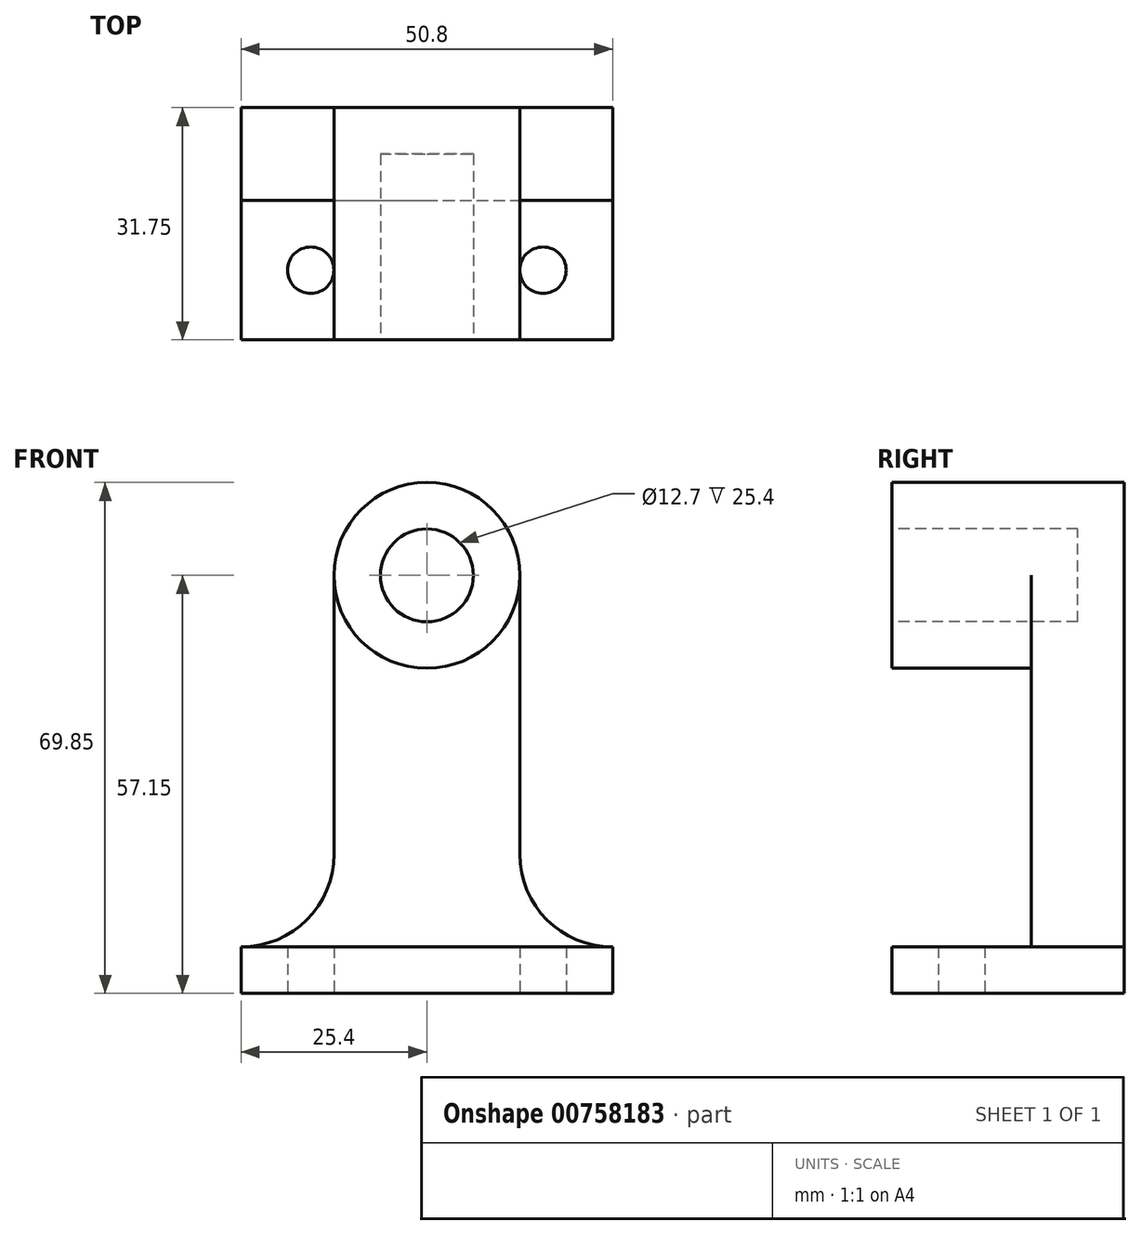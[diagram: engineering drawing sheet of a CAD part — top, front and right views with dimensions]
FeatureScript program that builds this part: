
annotation { "Feature Type Name" : "Feature", "Feature Type Description" : "" }
export const myFeature = defineFeature(function(context is Context, id is Id, definition is map)
    precondition{}
    {
        {
            var Q0;
            Q0=qCreatedBy(makeId("Top.planeOp"),FACE);
            var sketch = newSketch(context, id + "F0", { "sketchPlane" : qUnion([Q0])});
            skLineSegment(sketch, "E0", {"start": v(0, 0) * mm, "end": v(50.8, 0) * mm});
            skLineSegment(sketch, "E1", {"start": v(50.8, 0) * mm, "end": v(50.8, 31.75) * mm});
            skLineSegment(sketch, "E2", {"start": v(50.8, 31.75) * mm, "end": v(0, 31.75) * mm});
            skLineSegment(sketch, "E3", {"start": v(0, 31.75) * mm, "end": v(0, 0) * mm});
            skSolve(sketch);
        }
        {
            var Q0;
            Q0 = qSketchRegion(id + "F0", true);
            extrude(context, id + "F1", {"entities" : qUnion([Q0]), "depth" : 69.85 * mm, "offsetDistance" : 25.4 * mm});
        }
        {
            var Q0;
            Q0=makeQuery(id+"F1.opExtrude","SWEPT_FACE",FACE,{"disambiguationData":[OSD([sQuery(id+"F0.wireOp",EDGE,"E0")])]});
            var sketch = newSketch(context, id + "F2", { "sketchPlane" : qUnion([Q0])});
            skLineSegment(sketch, "E4", {"start": v(0, 6.35) * mm, "end": v(50.8, 6.35) * mm});
            skLineSegment(sketch, "E5", {"start": v(0, 44.45) * mm, "end": v(50.8, 44.45) * mm});
            skSolve(sketch);
        }
        {
            var Q0;
            Q0 = qSketchRegion(id + "F2", true);
            var Q1;
            {var subQ0=sQuery(id+"F2.wireOp",EDGE,"E4");Q1=makeQuery(id+"F2.imprint","IMPRINT",FACE,{"disambiguationData":[TD([[makeQuery(id+"F2.imprint","IMPRINT",EDGE,{"derivedFrom":subQ0}),1.0]])]});}
            extrude(context, id + "F3", {"entities" : qUnion([Q0, Q1]), "operationType" : NewBodyOperationType.REMOVE, "oppositeDirection" : true, "depth" : 19.05 * mm, "offsetDistance" : 25.4 * mm});
        }
        {
            var Q0;
            {var subQ2=sQuery(id+"F0.wireOp",EDGE,"E0");Q0=makeQuery(id+"F3.boolean.opBoolean","SPLIT",FACE,{"disambiguationData":[TD([makeQuery(id+"F3.opExtrude","SWEPT_FACE",FACE,{"disambiguationData":[OSD([sQuery(id+"F2.wireOp",EDGE,"E5")])]})])],"derivedFrom":makeQuery(id+"F1.opExtrude","SWEPT_FACE",FACE,{"disambiguationData":[OSD([subQ2])]})});}
            var sketch = newSketch(context, id + "F4", { "sketchPlane" : qUnion([Q0])});
            skCircle(sketch, "E6", {"center": v(25.4, 57.15) * mm, "radius": 12.7 * mm});
            skPoint(sketch, "E6.centerSnap0", {"position": v(0, 57.15) * mm});
            skCircle(sketch, "E7", {"center": v(25.4, 57.15) * mm, "radius": 6.35 * mm});
            skLineSegment(sketch, "E8", {"start": v(12.7, 57.15) * mm, "end": v(12.7, 19.05) * mm});
            skLineSegment(sketch, "E9", {"start": v(38.1, 57.15) * mm, "end": v(38.1, 19.05) * mm});
            skArc(sketch, "E10", {"start": v(38.1, 19.05) * mm, "mid": v(42.05, 10.1) * mm, "end": v(51.32, 6.98) * mm});
            skArc(sketch, "E11", {"start": v(0, 6.36) * mm, "mid": v(8.98, 10.07) * mm, "end": v(12.7, 19.05) * mm});
            skSolve(sketch);
        }
        {
            var Q0;
            {var subQ5=sQuery(id+"F4.wireOp",EDGE,"E6");var subQ7=sQuery(id+"F4.wireOp",EDGE,"E8");var subQ8=makeQuery(id+"F4.imprint","INTERSECT",VERTEX,{"derivedFrom":[subQ5,subQ7]});Q0=makeQuery(id+"F4.imprint","IMPRINT",FACE,{"disambiguationData":[TD([[makeQuery(id+"F4.imprint","IMPRINT",EDGE,{"disambiguationData":[TD([[subQ8,1.0]])],"derivedFrom":subQ5}),-1.0]])]});}
            var Q1;
            {var subQ4=sQuery(id+"F4.wireOp",EDGE,"E9");var subQ5=sQuery(id+"F4.wireOp",EDGE,"E6");var subQ6=makeQuery(id+"F4.imprint","INTERSECT",VERTEX,{"derivedFrom":[subQ5,subQ4]});Q1=makeQuery(id+"F4.imprint","IMPRINT",FACE,{"disambiguationData":[TD([[makeQuery(id+"F4.imprint","IMPRINT",EDGE,{"disambiguationData":[TD([[subQ6,-1.0]])],"derivedFrom":subQ5}),-1.0]])]});}
            var Q2;
            {var subQ0=sQuery(id+"F4.wireOp",EDGE,"E9");var subQ1=sQuery(id+"F4.wireOp",EDGE,"E6");var subQ2=makeQuery(id+"F4.imprint","INTERSECT",VERTEX,{"derivedFrom":[subQ1,subQ0]});Q2=makeQuery(id+"F4.imprint","IMPRINT",FACE,{"disambiguationData":[TD([[makeQuery(id+"F4.imprint","IMPRINT",EDGE,{"disambiguationData":[TD([[subQ2,1.0]])],"derivedFrom":subQ1}),-1.0]])]});}
            var Q3;
            {var subQ0=sQuery(id+"F4.wireOp",EDGE,"E8");var subQ1=sQuery(id+"F4.wireOp",EDGE,"E6");var subQ2=makeQuery(id+"F4.imprint","INTERSECT",VERTEX,{"derivedFrom":[subQ1,subQ0]});Q3=makeQuery(id+"F4.imprint","IMPRINT",FACE,{"disambiguationData":[TD([[makeQuery(id+"F4.imprint","IMPRINT",EDGE,{"disambiguationData":[TD([[subQ2,-1.0]])],"derivedFrom":subQ1}),-1.0]])]});}
            extrude(context, id + "F5", {"entities" : qUnion([Q0, Q1, Q2, Q3]), "operationType" : NewBodyOperationType.REMOVE, "oppositeDirection" : true, "depth" : 19.05 * mm, "offsetDistance" : 25.4 * mm});
        }
        {
            var Q0;
            {var subQ2=sQuery(id+"F0.wireOp",EDGE,"E0");Q0=makeQuery(id+"F3.boolean.opBoolean","SPLIT",FACE,{"disambiguationData":[TD([makeQuery(id+"F3.opExtrude","SWEPT_FACE",FACE,{"disambiguationData":[OSD([sQuery(id+"F2.wireOp",EDGE,"E5")])]})])],"derivedFrom":makeQuery(id+"F1.opExtrude","SWEPT_FACE",FACE,{"disambiguationData":[OSD([subQ2])]})});}
            var sketch = newSketch(context, id + "F6", { "sketchPlane" : qUnion([Q0])});
            skCircle(sketch, "E12", {"center": v(25.4, 57.15) * mm, "radius": 6.35 * mm});
            skSolve(sketch);
        }
        {
            var Q0;
            {var subQ0=sQuery(id+"F4.wireOp",EDGE,"E6");var subQ1=sQuery(id+"F2.wireOp",EDGE,"E5");var subQ2=sQuery(id+"F0.wireOp",EDGE,"E3");var subQ3=sQuery(id+"F0.wireOp",EDGE,"E0");var subQ4=sQuery(id+"F0.wireOp",EDGE,"E1");Q0=makeQuery(id+"F5.boolean.opBoolean","MERGE",FACE,{"derivedFrom":[makeQuery(id+"F3.boolean.opBoolean","COPY",FACE,{"derivedFrom":makeQuery(id+"F3.opExtrude","CAP_FACE",FACE,{"disambiguationData":[OSD([subQ3,subQ4,subQ2,sQuery(id+"F2.wireOp",EDGE,"E4"),subQ1])],"isStart":false})}),makeQuery(id+"F5.opExtrude","CAP_FACE",FACE,{"disambiguationData":[OSD([subQ3,subQ4,subQ1,subQ0])],"isStart":false}),makeQuery(id+"F5.opExtrude","CAP_FACE",FACE,{"disambiguationData":[OSD([subQ3,subQ2,subQ1,subQ0])],"isStart":false})]});}
            var sketch = newSketch(context, id + "F7", { "sketchPlane" : qUnion([Q0])});
            skLineSegment(sketch, "E13", {"start": v(25.4, 57.15) * mm, "end": v(38.1, 57.15) * mm});
            skLineSegment(sketch, "E14", {"start": v(38.1, 57.15) * mm, "end": v(38.1, 6.35) * mm});
            skLineSegment(sketch, "E15", {"start": v(25.4, 57.15) * mm, "end": v(12.7, 57.15) * mm});
            skLineSegment(sketch, "E16", {"start": v(12.7, 57.15) * mm, "end": v(12.7, 6.35) * mm});
            skArc(sketch, "E17", {"start": v(38.1, 19.05) * mm, "mid": v(41.82, 10.07) * mm, "end": v(50.8, 6.35) * mm});
            skArc(sketch, "E18", {"start": v(0, 6.35) * mm, "mid": v(8.98, 10.07) * mm, "end": v(12.7, 19.05) * mm});
            skSolve(sketch);
        }
        {
            var Q0;
            Q0 = qSketchRegion(id + "F7", true);
            var Q1;
            {var subQ11=sQuery(id+"F7.wireOp",EDGE,"E17");Q1=makeQuery(id+"F7.imprint","IMPRINT",FACE,{"disambiguationData":[TD([[makeQuery(id+"F7.imprint","IMPRINT",EDGE,{"derivedFrom":subQ11}),1.0]])]});}
            var Q2;
            {var subQ11=sQuery(id+"F7.wireOp",EDGE,"E18");Q2=makeQuery(id+"F7.imprint","IMPRINT",FACE,{"disambiguationData":[TD([[makeQuery(id+"F7.imprint","IMPRINT",EDGE,{"derivedFrom":subQ11}),1.0]])]});}
            var Q3;
            Q3=makeQuery(id+"F6.imprint","IMPRINT",FACE,{"disambiguationData":[TD([[makeQuery(id+"F6.imprint","IMPRINT",EDGE,{"derivedFrom":sQuery(id+"F6.wireOp",EDGE,"E12")}),1.0]])]});
            extrude(context, id + "F8", {"entities" : qUnion([Q0, Q1, Q2, Q3]), "operationType" : NewBodyOperationType.REMOVE, "oppositeDirection" : true, "depth" : 25.4 * mm, "offsetDistance" : 25.4 * mm});
        }
        {
            var Q0;
            Q0=qCreatedBy(makeId("Top.planeOp"),FACE);
            var sketch = newSketch(context, id + "F9", { "sketchPlane" : qUnion([Q0])});
            skCircle(sketch, "E19", {"center": v(9.53, 9.53) * mm, "radius": 3.18 * mm});
            skCircle(sketch, "E20", {"center": v(41.28, 9.53) * mm, "radius": 3.18 * mm});
            skSolve(sketch);
        }
        {
            var Q0;
            Q0=makeQuery(id+"F9.imprint","IMPRINT",FACE,{"disambiguationData":[TD([[makeQuery(id+"F9.imprint","IMPRINT",EDGE,{"derivedFrom":sQuery(id+"F9.wireOp",EDGE,"E20")}),1.0]])]});
            var Q1;
            Q1=makeQuery(id+"F9.imprint","IMPRINT",FACE,{"disambiguationData":[TD([[makeQuery(id+"F9.imprint","IMPRINT",EDGE,{"derivedFrom":sQuery(id+"F9.wireOp",EDGE,"E19")}),1.0]])]});
            extrude(context, id + "F10", {"entities" : qUnion([Q0, Q1]), "operationType" : NewBodyOperationType.REMOVE, "depth" : 19.05 * mm, "offsetDistance" : 25.4 * mm});
        }
    });
